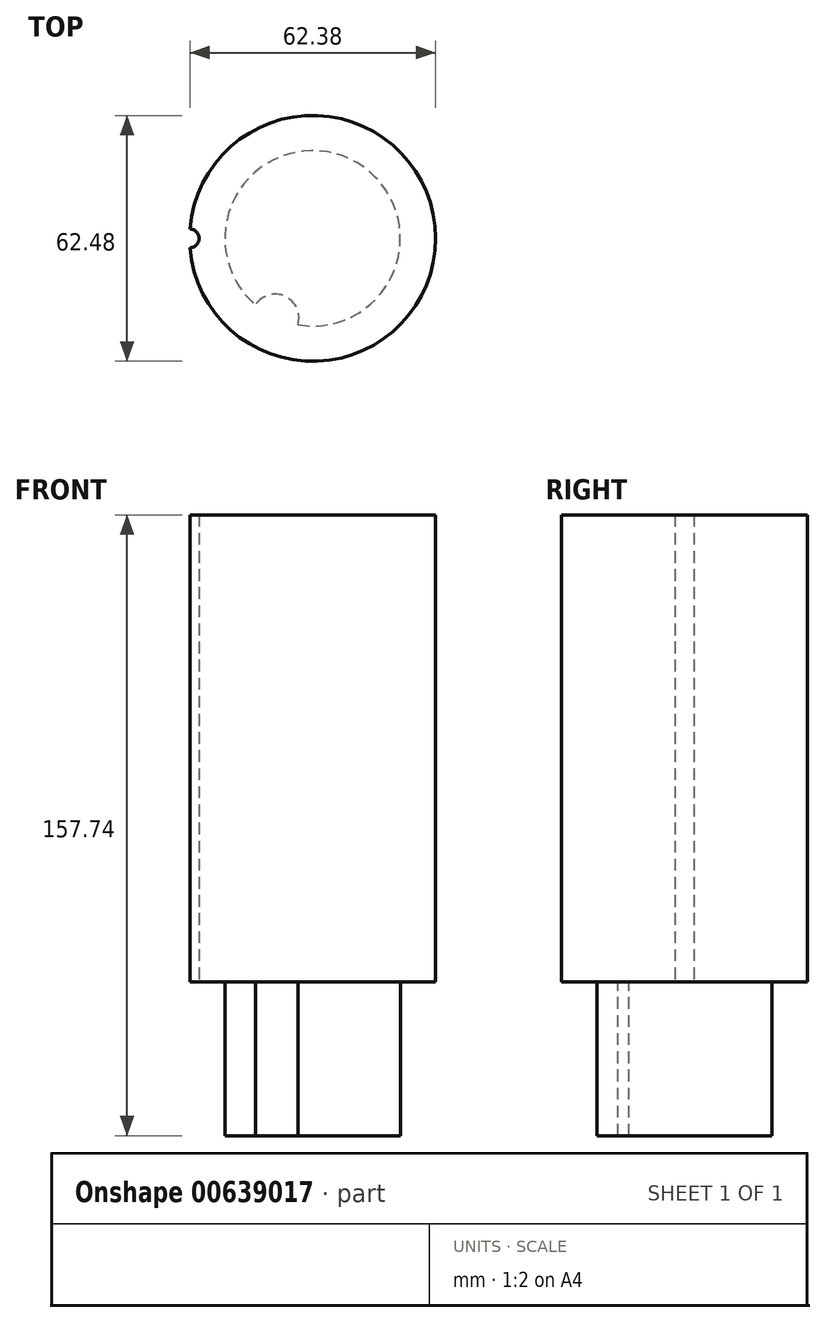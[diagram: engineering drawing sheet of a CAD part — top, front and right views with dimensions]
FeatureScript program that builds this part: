
annotation { "Feature Type Name" : "Feature", "Feature Type Description" : "" }
export const myFeature = defineFeature(function(context is Context, id is Id, definition is map)
    precondition{}
    {
        {
            var Q0;
            Q0=qCreatedBy(makeId("Top.planeOp"),FACE);
            var sketch = newSketch(context, id + "F0", { "sketchPlane" : qUnion([Q0])});
            skCircle(sketch, "E0", {"center": v(0, 0) * mm, "radius": 31.24 * mm});
            skCircle(sketch, "E1", {"center": v(-31.24, 0) * mm, "radius": 2.39 * mm});
            skSolve(sketch);
        }
        {
            var Q0;
            {var subQ0=sQuery(id+"F0.wireOp",EDGE,"E1");var subQ1=sQuery(id+"F0.wireOp",EDGE,"E0");var subQ2=makeQuery(id+"F0.imprint","INTERSECT",VERTEX,{"disambiguationData":[OD(0.0)],"derivedFrom":[subQ1,subQ0]});Q0=makeQuery(id+"F0.imprint","IMPRINT",FACE,{"disambiguationData":[TD([[makeQuery(id+"F0.imprint","IMPRINT",EDGE,{"disambiguationData":[TD([[subQ2,-1.0]])],"derivedFrom":subQ1}),1.0]])]});}
            extrude(context, id + "F1", {"entities" : qUnion([Q0]), "depth" : 118.62 * mm, "offsetDistance" : 25.4 * mm});
        }
        {
            var Q0;
            Q0=makeQuery(id+"F1.opExtrude","CAP_FACE",FACE,{"disambiguationData":[OSD([sQuery(id+"F0.wireOp",EDGE,"E0"),sQuery(id+"F0.wireOp",EDGE,"E1")])],"isStart":true});
            var sketch = newSketch(context, id + "F2", { "sketchPlane" : qUnion([Q0])});
            skCircle(sketch, "E2", {"center": v(0, 0) * mm, "radius": 22.28 * mm});
            skCircle(sketch, "E3", {"center": v(-9.48, 20.16) * mm, "radius": 6 * mm});
            skSolve(sketch);
        }
        {
            var Q0;
            {var subQ0=sQuery(id+"F2.wireOp",EDGE,"E3");var subQ1=sQuery(id+"F2.wireOp",EDGE,"E2");var subQ2=makeQuery(id+"F2.imprint","INTERSECT",VERTEX,{"disambiguationData":[OD(0.0)],"derivedFrom":[subQ1,subQ0]});Q0=makeQuery(id+"F2.imprint","IMPRINT",FACE,{"disambiguationData":[TD([[makeQuery(id+"F2.imprint","IMPRINT",EDGE,{"disambiguationData":[TD([[subQ2,-1.0]])],"derivedFrom":subQ1}),1.0]])]});}
            extrude(context, id + "F3", {"entities" : qUnion([Q0]), "operationType" : NewBodyOperationType.ADD, "depth" : 39.12 * mm, "offsetDistance" : 25.4 * mm});
        }
    });
